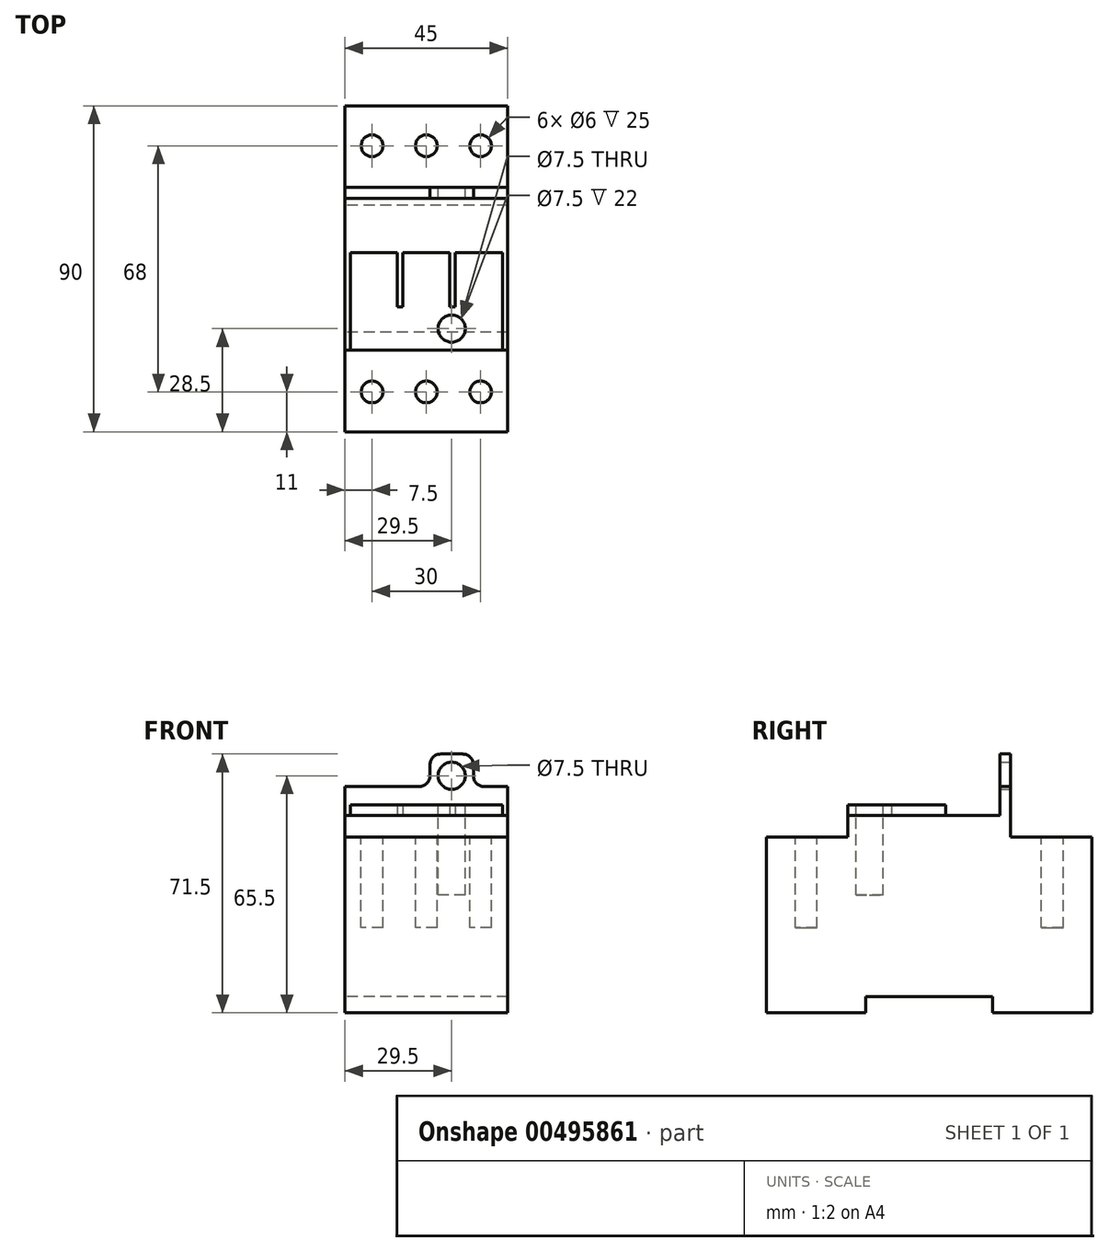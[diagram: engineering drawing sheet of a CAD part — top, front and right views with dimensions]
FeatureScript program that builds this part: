
annotation { "Feature Type Name" : "Feature", "Feature Type Description" : "" }
export const myFeature = defineFeature(function(context is Context, id is Id, definition is map)
    precondition{}
    {
        {
            var Q0;
            Q0=qCreatedBy(makeId("Right.planeOp"),FACE);
            var sketch = newSketch(context, id + "F0", { "sketchPlane" : qUnion([Q0])});
            skLineSegment(sketch, "E0", {"start": v(-45, -4.5) * mm, "end": v(-17.5, -4.5) * mm});
            skLineSegment(sketch, "E1", {"start": v(-17.5, -4.5) * mm, "end": v(-17.5, 0) * mm});
            skLineSegment(sketch, "E2", {"start": v(-17.5, 0) * mm, "end": v(17.5, 0) * mm});
            skLineSegment(sketch, "E3", {"start": v(17.5, 0) * mm, "end": v(17.5, -4.5) * mm});
            skLineSegment(sketch, "E4", {"start": v(17.5, -4.5) * mm, "end": v(45, -4.5) * mm});
            skLineSegment(sketch, "E5", {"start": v(45, -4.5) * mm, "end": v(45, 44) * mm});
            skLineSegment(sketch, "E6", {"start": v(45, 44) * mm, "end": v(22.5, 44) * mm});
            skLineSegment(sketch, "E7", {"start": v(22.5, 44) * mm, "end": v(22.5, 67) * mm});
            skLineSegment(sketch, "E8", {"start": v(22.5, 67) * mm, "end": v(19.5, 67) * mm});
            skLineSegment(sketch, "E9", {"start": v(19.5, 67) * mm, "end": v(19.5, 50) * mm});
            skLineSegment(sketch, "E10", {"start": v(19.5, 50) * mm, "end": v(-22.5, 50) * mm});
            skLineSegment(sketch, "E11", {"start": v(-22.5, 50) * mm, "end": v(-22.5, 44) * mm});
            skLineSegment(sketch, "E12", {"start": v(-22.5, 44) * mm, "end": v(-45, 44) * mm});
            skLineSegment(sketch, "E13", {"start": v(-45, 44) * mm, "end": v(-45, -4.5) * mm});
            skSolve(sketch);
        }
        {
            var Q0;
            Q0=qSketchRegion(id+"F0",true);
            extrude(context, id + "F1", {"entities" : qUnion([Q0]), "endBound" : BoundingType.SYMMETRIC, "depth" : 45 * mm});
        }
        {
            var Q0;
            Q0=makeQuery(id+"F1.opExtrude","SWEPT_FACE",FACE,{"disambiguationData":[OSD([sQuery(id+"F0.wireOp",EDGE,"E7")])]});
            var sketch = newSketch(context, id + "F2", { "sketchPlane" : qUnion([Q0])});
            skCircle(sketch, "E14", {"center": v(-7, 61) * mm, "radius": 3.75 * mm});
            skLineSegment(sketch, "E15", {"start": v(-13, 64) * mm, "end": v(-13, 61) * mm});
            skLineSegment(sketch, "E16", {"start": v(-16, 58) * mm, "end": v(-22.5, 58) * mm});
            skLineSegment(sketch, "E17", {"start": v(-10, 67) * mm, "end": v(-4, 67) * mm});
            skLineSegment(sketch, "E18", {"start": v(-1, 64) * mm, "end": v(-1, 61) * mm});
            skLineSegment(sketch, "E19", {"start": v(2, 58) * mm, "end": v(22.5, 58) * mm});
            skLineSegment(sketch, "E20", {"start": v(22.5, 58) * mm, "end": v(37.24, 58) * mm});
            skLineSegment(sketch, "E21", {"start": v(37.24, 58) * mm, "end": v(37.24, 73.09) * mm});
            skLineSegment(sketch, "E22", {"start": v(37.24, 73.09) * mm, "end": v(-27.59, 73.09) * mm});
            skLineSegment(sketch, "E23", {"start": v(-27.59, 73.09) * mm, "end": v(-27.59, 58) * mm});
            skLineSegment(sketch, "E24", {"start": v(-27.59, 58) * mm, "end": v(-22.5, 58) * mm});
            skPoint(sketch, "E25.visualSharp", {"position": v(-13, 67) * mm});
            skArc(sketch, "E25.filletArc", {"start": v(-10, 67) * mm, "mid": v(-12.12, 66.12) * mm, "end": v(-13, 64) * mm});
            skPoint(sketch, "E26.visualSharp", {"position": v(-1, 67) * mm});
            skArc(sketch, "E26.filletArc", {"start": v(-1, 64) * mm, "mid": v(-1.88, 66.12) * mm, "end": v(-4, 67) * mm});
            skPoint(sketch, "E27.visualSharp", {"position": v(-1, 58) * mm});
            skArc(sketch, "E27.filletArc", {"start": v(-1, 61) * mm, "mid": v(-0.12, 58.88) * mm, "end": v(2, 58) * mm});
            skPoint(sketch, "E28.visualSharp", {"position": v(-13, 58) * mm});
            skArc(sketch, "E28.filletArc", {"start": v(-16, 58) * mm, "mid": v(-13.88, 58.88) * mm, "end": v(-13, 61) * mm});
            skSolve(sketch);
        }
        {
            var Q0;
            Q0=qSketchRegion(id+"F2",true);
            extrude(context, id + "F3", {"entities" : qUnion([Q0]), "operationType" : NewBodyOperationType.REMOVE, "oppositeDirection" : true, "depth" : 25 * mm});
        }
        {
            var Q0;
            Q0=makeQuery(id+"F1.opExtrude","SWEPT_FACE",FACE,{"disambiguationData":[OSD([sQuery(id+"F0.wireOp",EDGE,"E10")])]});
            var sketch = newSketch(context, id + "F4", { "sketchPlane" : qUnion([Q0])});
            skLineSegment(sketch, "E29", {"start": v(21, -22.5) * mm, "end": v(-21, -22.5) * mm});
            skLineSegment(sketch, "E30", {"start": v(-21, -22.5) * mm, "end": v(-21, 4.5) * mm});
            skLineSegment(sketch, "E31", {"start": v(-21, 4.5) * mm, "end": v(-8, 4.5) * mm});
            skLineSegment(sketch, "E32", {"start": v(-8, 4.5) * mm, "end": v(-8, -10.5) * mm});
            skLineSegment(sketch, "E33", {"start": v(-8, -10.5) * mm, "end": v(-6.5, -10.5) * mm});
            skLineSegment(sketch, "E34", {"start": v(-6.5, -10.5) * mm, "end": v(-6.5, 4.5) * mm});
            skLineSegment(sketch, "E35", {"start": v(-6.5, 4.5) * mm, "end": v(6.5, 4.5) * mm});
            skLineSegment(sketch, "E36", {"start": v(6.5, 4.5) * mm, "end": v(6.5, -10.5) * mm});
            skLineSegment(sketch, "E37", {"start": v(6.5, -10.5) * mm, "end": v(8, -10.5) * mm});
            skLineSegment(sketch, "E38", {"start": v(8, -10.5) * mm, "end": v(8, 4.5) * mm});
            skLineSegment(sketch, "E39", {"start": v(8, 4.5) * mm, "end": v(21, 4.5) * mm});
            skLineSegment(sketch, "E40", {"start": v(21, 4.5) * mm, "end": v(21, -22.5) * mm});
            skSolve(sketch);
        }
        {
            var Q0;
            Q0=qSketchRegion(id+"F4",true);
            extrude(context, id + "F5", {"entities" : qUnion([Q0]), "depth" : 3 * mm});
        }
        {
            var Q0;
            Q0=makeQuery(id+"F1.opExtrude","SWEPT_FACE",FACE,{"disambiguationData":[OSD([sQuery(id+"F0.wireOp",EDGE,"E6")])]});
            var sketch = newSketch(context, id + "F6", { "sketchPlane" : qUnion([Q0])});
            skCircle(sketch, "E41", {"center": v(15, -34) * mm, "radius": 3 * mm});
            skCircle(sketch, "E42.MirrorC", {"center": v(-15, -34) * mm, "radius": 3 * mm});
            skLineSegment(sketch, "E43", {"start": v(15, -34) * mm, "end": v(-15, -34) * mm, "construction": true});
            skCircle(sketch, "E44", {"center": v(0, -34) * mm, "radius": 3 * mm});
            skCircle(sketch, "E45.MirrorC", {"center": v(-15, 34) * mm, "radius": 3 * mm});
            skCircle(sketch, "E46.MirrorC", {"center": v(0, 34) * mm, "radius": 3 * mm});
            skCircle(sketch, "E47.MirrorC", {"center": v(15, 34) * mm, "radius": 3 * mm});
            skSolve(sketch);
        }
        {
            var Q0;
            Q0=qSketchRegion(id+"F6",true);
            extrude(context, id + "F7", {"entities" : qUnion([Q0]), "operationType" : NewBodyOperationType.REMOVE, "oppositeDirection" : true, "depth" : 25 * mm});
        }
        {
            var Q0;
            Q0=makeQuery(id+"F5.opExtrude","CAP_FACE",FACE,{"disambiguationData":[OSD([sQuery(id+"F4.wireOp",EDGE,"E29"),sQuery(id+"F4.wireOp",EDGE,"E30"),sQuery(id+"F4.wireOp",EDGE,"E31"),sQuery(id+"F4.wireOp",EDGE,"E32"),sQuery(id+"F4.wireOp",EDGE,"E33"),sQuery(id+"F4.wireOp",EDGE,"E34"),sQuery(id+"F4.wireOp",EDGE,"E35"),sQuery(id+"F4.wireOp",EDGE,"E36"),sQuery(id+"F4.wireOp",EDGE,"E37"),sQuery(id+"F4.wireOp",EDGE,"E38"),sQuery(id+"F4.wireOp",EDGE,"E39"),sQuery(id+"F4.wireOp",EDGE,"E40")])],"isStart":false});
            var sketch = newSketch(context, id + "F8", { "sketchPlane" : qUnion([Q0])});
            skCircle(sketch, "E48", {"center": v(7, -16.5) * mm, "radius": 3.75 * mm});
            skSolve(sketch);
        }
        {
            var Q0;
            Q0=qSketchRegion(id+"F8",true);
            extrude(context, id + "F9", {"entities" : qUnion([Q0]), "operationType" : NewBodyOperationType.REMOVE, "oppositeDirection" : true, "depth" : 25 * mm});
        }
    });
